# Revit family: E_Cable Tray Support_MEPcontent_OBO Bettermann_SL 62 FT
name_source: partatom
category: Cable Tray Fittings
revit_build: Autodesk Revit MEP 2015 (Build: 20140606_1530(x64)
units: mm (PartAtom-declared; Revit-internal decimal feet)

## types (1)
- SLH 62 FT
    Article Description = Perforated side rail of ship cable ladder, SL 62, for creation of suspension and support structures.
    Article Type = SLH 62 FT
    Description = Perforated side rail of ship cable ladder, SL 62, for creation of suspension and support structures.
    EMCS Version = 2.0
    ETIM Article Class = EC001005
    Family Version = 10.14
    GTIN = 4012196468911
    Gray = Color RGB 189-187-185
    IFCExportAs = IfcCableCarrierFittingType
    IFCExportType = NOTDEFINED
    Length = 3000 mm  [stored 9.84252 ft]
    MEPcontent Class = CABLE_TRAY_SUPPORT
    Manufacturer = OBO BETTERMANN
    Manufacturer Art. No. = 7103643
    Manufacturer URL = http://catalog4.obo-bettermann.com
    Model = SLH 62 FT
    Product Line = OBO BETTERMANN CableTrays
    Revit Version = 2015
    URL = www.stabiplan.com
    Width 1 = 40 mm  [stored 0.131234 ft]

note: [stored X ft] marks values corroborated as IEEE doubles in the binary element streams (Revit-internal decimal feet)

## geometry (parser evidence)
native form markers: Blend x4, Sweep x3
no freeform markers — native parametric forms only
